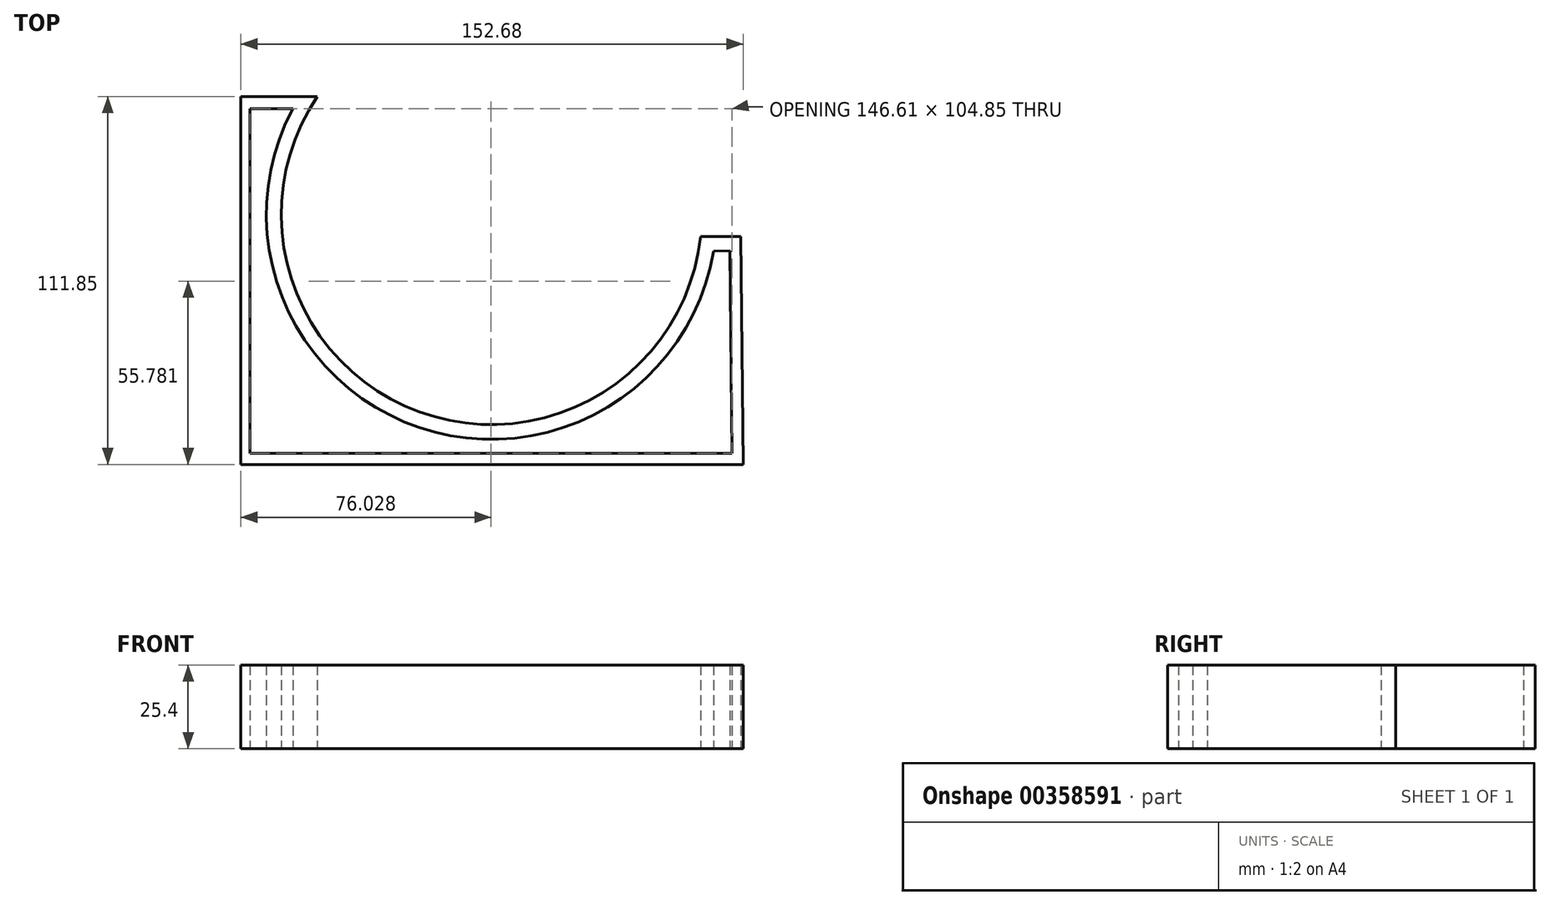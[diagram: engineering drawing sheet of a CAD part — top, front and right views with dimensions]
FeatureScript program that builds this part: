
annotation { "Feature Type Name" : "Feature", "Feature Type Description" : "" }
export const myFeature = defineFeature(function(context is Context, id is Id, definition is map)
    precondition{}
    {
        {
            var Q0;
            Q0=qCreatedBy(makeId("Top.planeOp"),FACE);
            var sketch = newSketch(context, id + "F0", { "sketchPlane" : qUnion([Q0])});
            skArc(sketch, "E0", {"start": v(-52.95, 35.8) * mm, "mid": v(-21.9, -60.05) * mm, "end": v(63.56, -6.68) * mm});
            skLineSegment(sketch, "E1", {"start": v(-76.18, 35.8) * mm, "end": v(-52.95, 35.8) * mm});
            skLineSegment(sketch, "E2", {"start": v(63.56, -6.68) * mm, "end": v(75.76, -6.68) * mm});
            skPoint(sketch, "E3.start.orphan", {"position": v(0, 67.89) * mm});
            skLineSegment(sketch, "E4", {"start": v(-76.18, 35.8) * mm, "end": v(-76.18, -76.05) * mm});
            skLineSegment(sketch, "E5", {"start": v(-76.18, -76.05) * mm, "end": v(76.5, -76.05) * mm});
            skLineSegment(sketch, "E6", {"start": v(76.5, -76.05) * mm, "end": v(75.76, -6.68) * mm});
            skLineSegment(sketch, "E7", {"start": v(-73.46, 32.16) * mm, "end": v(-60.4, 32.16) * mm});
            skLineSegment(sketch, "E8", {"start": v(-73.46, 32.16) * mm, "end": v(-73.46, -72.7) * mm});
            skLineSegment(sketch, "E9", {"start": v(-73.46, -72.7) * mm, "end": v(73.15, -72.7) * mm});
            skLineSegment(sketch, "E10", {"start": v(73.15, -72.7) * mm, "end": v(72.5, -11.1) * mm});
            skLineSegment(sketch, "E11", {"start": v(72.5, -11.1) * mm, "end": v(67.51, -11.16) * mm});
            skArc(sketch, "E12", {"start": v(-60.4, 32.16) * mm, "mid": v(-21.95, -64.81) * mm, "end": v(67.51, -11.16) * mm});
            skPoint(sketch, "E13.start.orphan", {"position": v(0, 73.3) * mm});
            skSolve(sketch);
        }
        {
            var Q0;
            Q0 = qSketchRegion(id + "F0", true);
            extrude(context, id + "F1", {"entities" : qUnion([Q0]), "depth" : 25.4 * mm});
        }
    });
